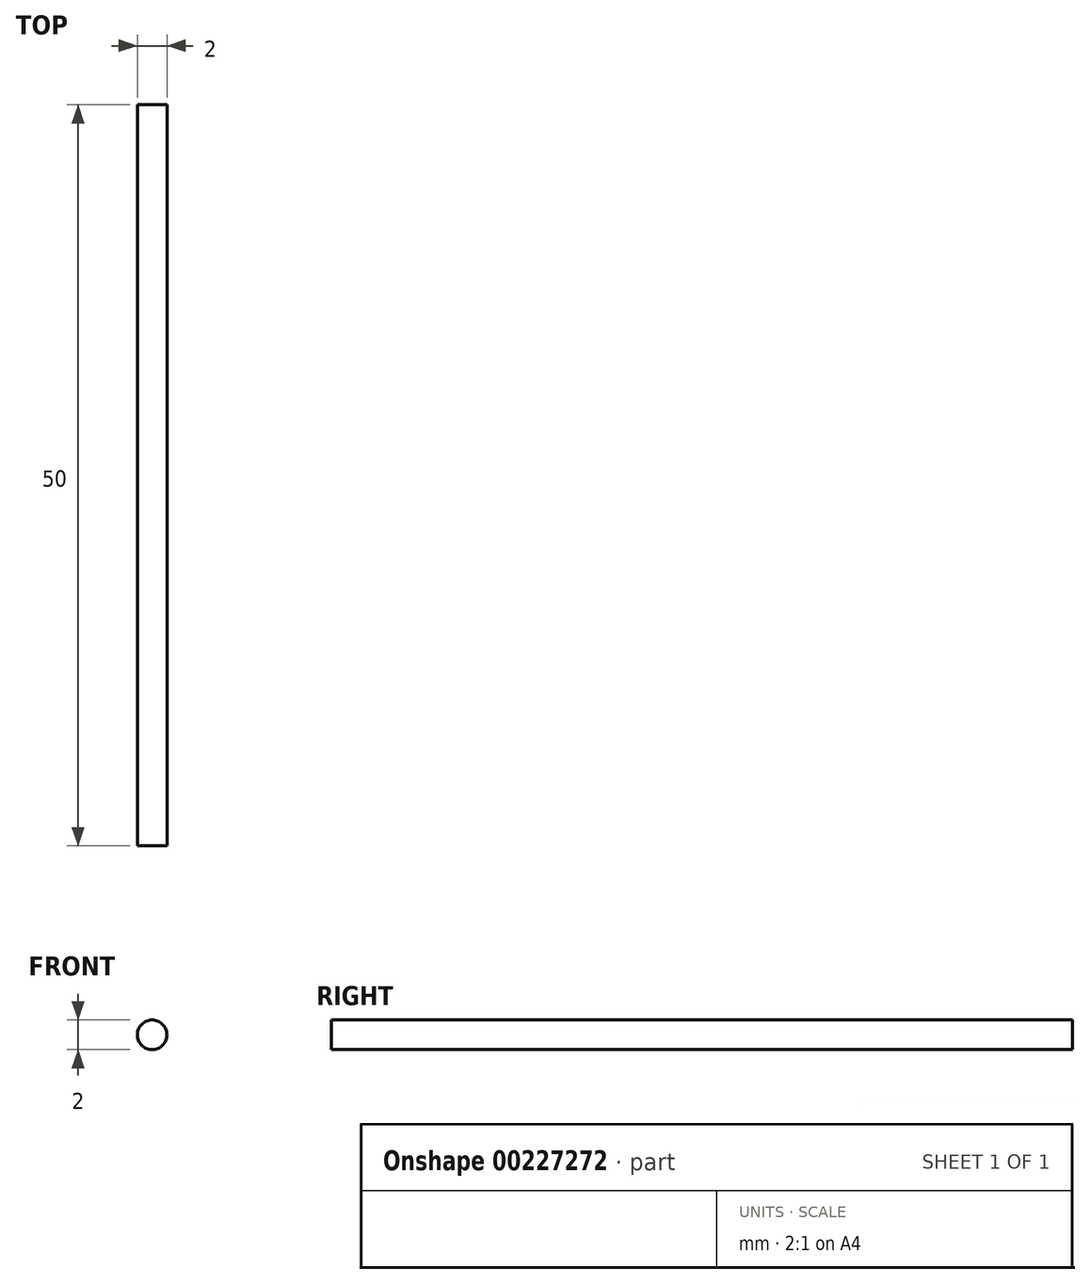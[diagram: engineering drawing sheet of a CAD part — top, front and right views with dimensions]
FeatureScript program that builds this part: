
annotation { "Feature Type Name" : "Feature", "Feature Type Description" : "" }
export const myFeature = defineFeature(function(context is Context, id is Id, definition is map)
    precondition{}
    {
        {
            var Q0;
            Q0=qCreatedBy(makeId("Front.planeOp"),FACE);
            var sketch = newSketch(context, id + "F0", { "sketchPlane" : qUnion([Q0])});
            skCircle(sketch, "E0", {"center": v(0, 0) * mm, "radius": 1 * mm});
            skSolve(sketch);
        }
        {
            var Q0;
            Q0 = qSketchRegion(id + "F0", true);
            extrude(context, id + "F1", {"entities" : qUnion([Q0]), "depth" : 50 * mm});
        }
    });
